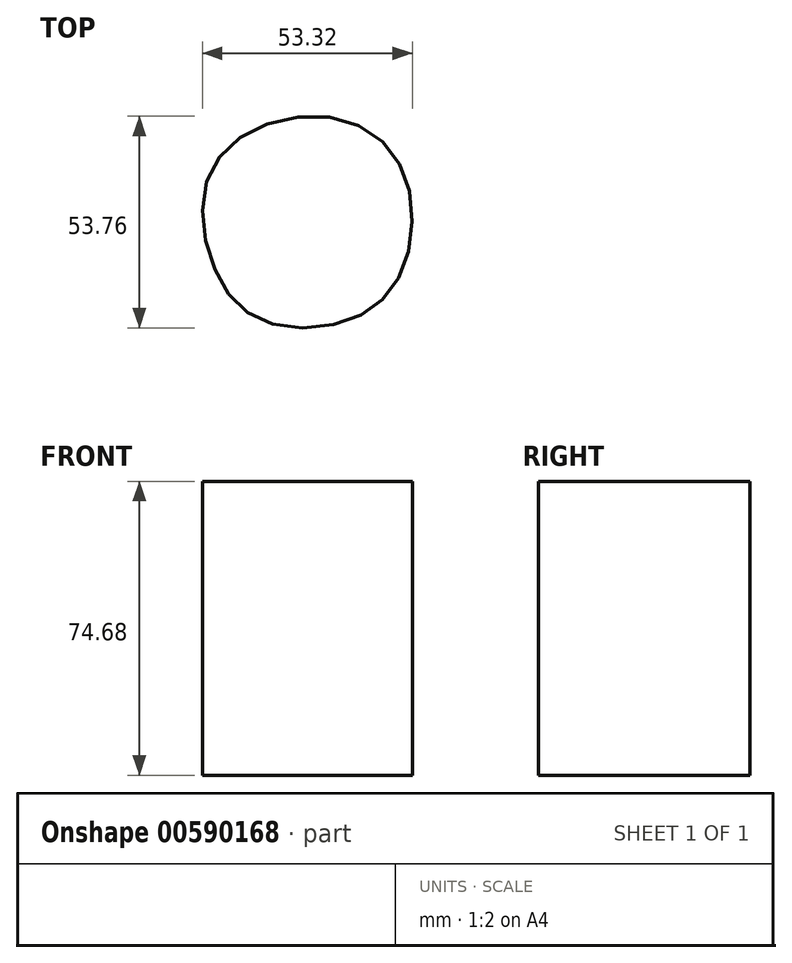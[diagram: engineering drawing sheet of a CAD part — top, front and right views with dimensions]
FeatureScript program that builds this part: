
annotation { "Feature Type Name" : "Feature", "Feature Type Description" : "" }
export const myFeature = defineFeature(function(context is Context, id is Id, definition is map)
    precondition{}
    {
        {
            var Q0;
            Q0=qCreatedBy(makeId("Top.planeOp"),FACE);
            var sketch = newSketch(context, id + "F0", { "sketchPlane" : qUnion([Q0])});
            skFitSpline(sketch, "E0", {"points": [v(-60.62, -22.14) * mm, v(-62.76, 0) * mm, v(-49.01, 14.2) * mm, v(-24.89, 14.81) * mm, v(-11.76, 0) * mm, v(-12.98, -22.14) * mm, v(-25.5, -34.66) * mm, v(-48.1, -35.27) * mm, v(-60.62, -22.14) * mm]});
            skSolve(sketch);
        }
        {
            var Q0;
            Q0=makeQuery(id+"F0.imprint","IMPRINT",FACE,{"disambiguationData":[TD([[makeQuery(id+"F0.imprint","IMPRINT",EDGE,{"derivedFrom":sQuery(id+"F0.wireOp",EDGE,"E0")}),-1.0]])]});
            extrude(context, id + "F1", {"entities" : qUnion([Q0]), "depth" : 74.68 * mm, "offsetDistance" : 25.4 * mm});
        }
    });
